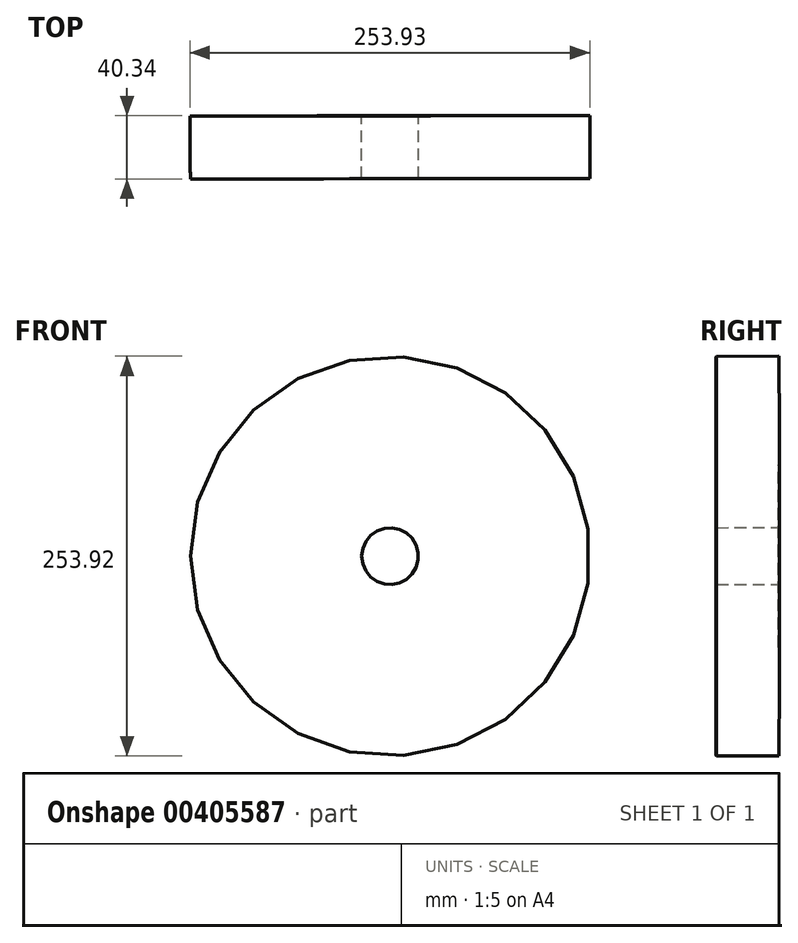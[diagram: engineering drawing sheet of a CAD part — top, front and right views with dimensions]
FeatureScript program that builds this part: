
annotation { "Feature Type Name" : "Feature", "Feature Type Description" : "" }
export const myFeature = defineFeature(function(context is Context, id is Id, definition is map)
    precondition{}
    {
        {
            var Q0;
            Q0=qCreatedBy(makeId("Top.planeOp"),FACE);
            var sketch = newSketch(context, id + "F0", { "sketchPlane" : qUnion([Q0])});
            skLineSegment(sketch, "E0.bottom", {"start": v(-50.9, 50.9) * mm, "end": v(57.99, 50.9) * mm});
            skLineSegment(sketch, "E0.top", {"start": v(-50.9, 11.01) * mm, "end": v(57.99, 11.01) * mm});
            skLineSegment(sketch, "E0.left", {"start": v(-50.9, 50.9) * mm, "end": v(-50.9, 11.01) * mm});
            skLineSegment(sketch, "E0.right", {"start": v(57.99, 50.9) * mm, "end": v(57.99, 11.01) * mm});
            skLineSegment(sketch, "E1.bottom", {"start": v(-45.27, 11.01) * mm, "end": v(52.85, 11.01) * mm});
            skLineSegment(sketch, "E1.top", {"start": v(-45.27, -48.2) * mm, "end": v(52.85, -48.2) * mm});
            skLineSegment(sketch, "E1.left", {"start": v(-45.27, 11.01) * mm, "end": v(-45.27, -48.2) * mm});
            skLineSegment(sketch, "E1.right", {"start": v(52.85, 11.01) * mm, "end": v(52.85, -48.2) * mm});
            skLineSegment(sketch, "E2.bottom", {"start": v(-34.99, -48.2) * mm, "end": v(46.98, -48.2) * mm});
            skLineSegment(sketch, "E2.top", {"start": v(-34.99, -69.49) * mm, "end": v(46.98, -69.49) * mm});
            skLineSegment(sketch, "E2.left", {"start": v(-34.99, -48.2) * mm, "end": v(-34.99, -69.49) * mm});
            skLineSegment(sketch, "E2.right", {"start": v(46.98, -48.2) * mm, "end": v(46.98, -69.49) * mm});
            skLineSegment(sketch, "E3.bottom", {"start": v(-68.75, 64.35) * mm, "end": v(-69, 64.35) * mm});
            skLineSegment(sketch, "E3.top", {"start": v(-68.75, -69.49) * mm, "end": v(-69, -69.49) * mm});
            skLineSegment(sketch, "E4", {"start": v(-69, 64.35) * mm, "end": v(-68.75, -69.49) * mm});
            skSolve(sketch);
        }
        {
            var Q0;
            Q0=makeQuery(id+"F0.imprint","IMPRINT",FACE,{"disambiguationData":[TD([[makeQuery(id+"F0.imprint","IMPRINT",EDGE,{"derivedFrom":sQuery(id+"F0.wireOp",EDGE,"E1.bottom")}),-1.0]])]});
            var Q1;
            Q1=makeQuery(id+"F0.imprint","IMPRINT",FACE,{"disambiguationData":[TD([[makeQuery(id+"F0.imprint","IMPRINT",EDGE,{"derivedFrom":sQuery(id+"F0.wireOp",EDGE,"E2.bottom")}),-1.0]])]});
            var Q2;
            Q2=makeQuery(id+"F0.imprint","IMPRINT",FACE,{"disambiguationData":[TD([[makeQuery(id+"F0.imprint","IMPRINT",EDGE,{"derivedFrom":sQuery(id+"F0.wireOp",EDGE,"E0.bottom")}),-1.0]])]});
            var Q3;
            Q3=sQuery(id+"F0.wireOp",EDGE,"E4");
            revolve(context, id + "F1", {"entities" : qUnion([Q0, Q1, Q2]), "axis" : qUnion([Q3]), "revolveType" : RevolveType.FULL});
        }
    });
